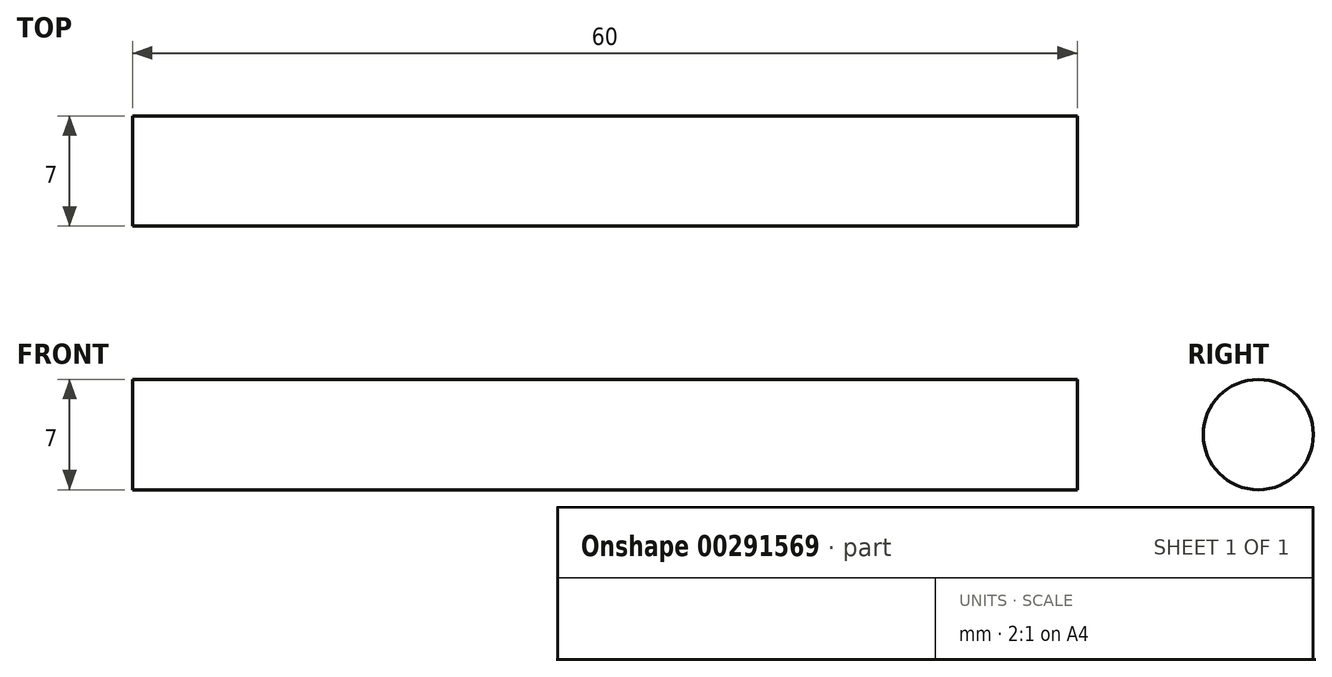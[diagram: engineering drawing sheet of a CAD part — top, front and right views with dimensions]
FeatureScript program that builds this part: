
annotation { "Feature Type Name" : "Feature", "Feature Type Description" : "" }
export const myFeature = defineFeature(function(context is Context, id is Id, definition is map)
    precondition{}
    {
        {
            var Q0;
            Q0=qCreatedBy(makeId("Right.planeOp"),FACE);
            var sketch = newSketch(context, id + "F0", { "sketchPlane" : qUnion([Q0])});
            skCircle(sketch, "E0", {"center": v(0, 0) * mm, "radius": 3.5 * mm});
            skSolve(sketch);
        }
        {
            var Q0;
            Q0 = qSketchRegion(id + "F0", true);
            extrude(context, id + "F1", {"entities" : qUnion([Q0]), "endBound" : BoundingType.SYMMETRIC, "depth" : 60 * mm});
        }
    });
